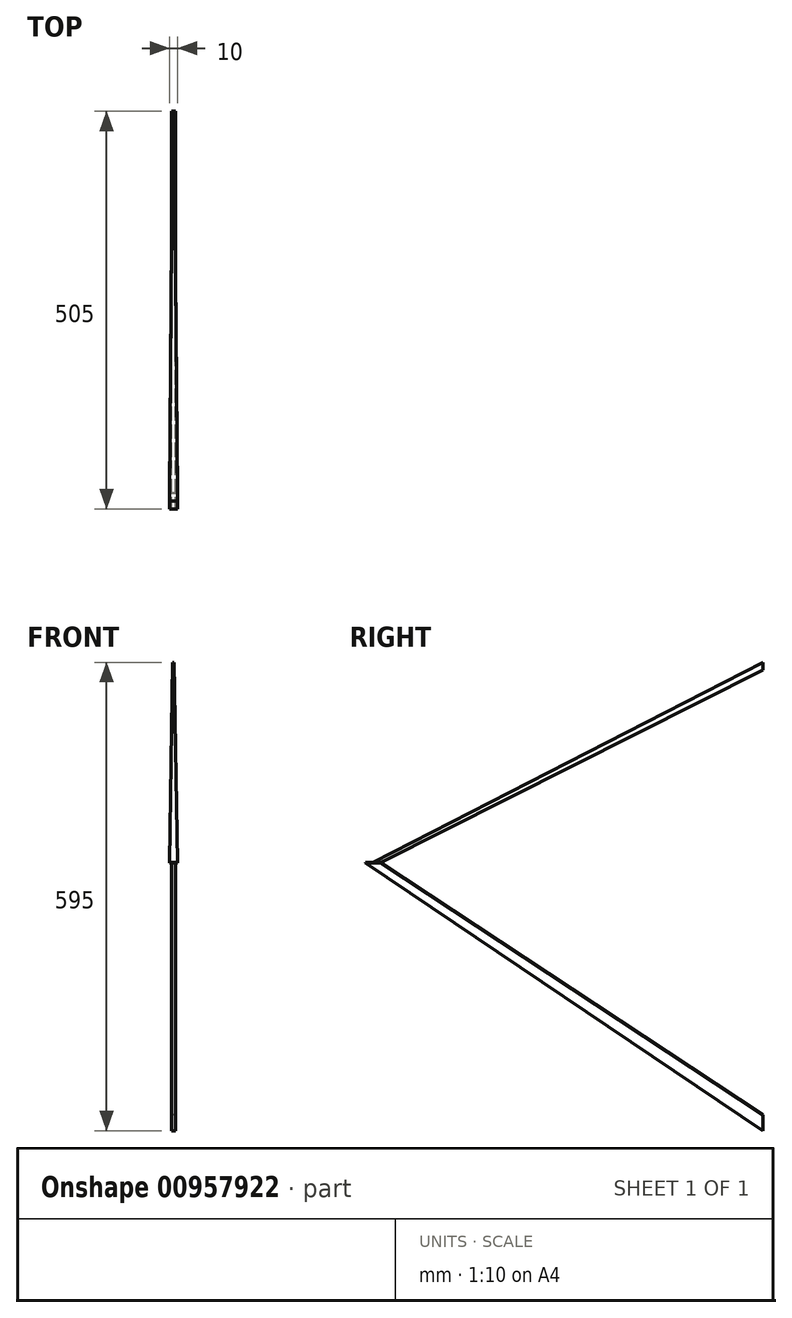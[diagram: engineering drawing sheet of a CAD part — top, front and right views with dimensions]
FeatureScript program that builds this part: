
annotation { "Feature Type Name" : "Feature", "Feature Type Description" : "" }
export const myFeature = defineFeature(function(context is Context, id is Id, definition is map)
    precondition{}
    {
        {
            var Q0;
            Q0=qCreatedBy(makeId("Top.planeOp"),FACE);
            var sketch = newSketch(context, id + "F0", { "sketchPlane" : qUnion([Q0])});
            skLineSegment(sketch, "E0.bottom", {"start": v(-49.59, 0) * mm, "end": v(-39.59, 0) * mm});
            skLineSegment(sketch, "E0.top", {"start": v(-49.59, -505) * mm, "end": v(-39.59, -505) * mm});
            skLineSegment(sketch, "E0.left", {"start": v(-49.59, 0) * mm, "end": v(-49.59, -505) * mm});
            skLineSegment(sketch, "E0.right", {"start": v(-39.59, 0) * mm, "end": v(-39.59, -505) * mm});
            skSolve(sketch);
        }
        {
            var Q0;
            Q0 = qSketchRegion(id + "F0", true);
            extrude(context, id + "F1", {"entities" : qUnion([Q0]), "depth" : 1 * mm, "offsetDistance" : 25 * mm});
        }
        {
            var Q0;
            Q0=makeQuery(id+"F1.opExtrude","CAP_FACE",FACE,{"disambiguationData":[OSD([sQuery(id+"F0.wireOp",EDGE,"E0.bottom"),sQuery(id+"F0.wireOp",EDGE,"E0.top"),sQuery(id+"F0.wireOp",EDGE,"E0.left"),sQuery(id+"F0.wireOp",EDGE,"E0.right")])],"isStart":false});
            var sketch = newSketch(context, id + "F2", { "sketchPlane" : qUnion([Q0])});
            skLineSegment(sketch, "E1.bottom", {"start": v(-49.59, -505) * mm, "end": v(-39.59, -505) * mm});
            skLineSegment(sketch, "E1.top", {"start": v(-49.59, -495) * mm, "end": v(-39.59, -495) * mm});
            skLineSegment(sketch, "E1.left", {"start": v(-49.59, -505) * mm, "end": v(-49.59, -495) * mm});
            skLineSegment(sketch, "E1.right", {"start": v(-39.59, -505) * mm, "end": v(-39.59, -495) * mm});
            skSolve(sketch);
        }
        {
            var Q0;
            Q0=makeQuery(id+"F1.opExtrude","CAP_FACE",FACE,{"disambiguationData":[OSD([sQuery(id+"F0.wireOp",EDGE,"E0.bottom"),sQuery(id+"F0.wireOp",EDGE,"E0.top"),sQuery(id+"F0.wireOp",EDGE,"E0.left"),sQuery(id+"F0.wireOp",EDGE,"E0.right")])],"isStart":true});
            var sketch = newSketch(context, id + "F3", { "sketchPlane" : qUnion([Q0])});
            skLineSegment(sketch, "E2.bottom", {"start": v(-41.87, 505) * mm, "end": v(-47.3, 505) * mm});
            skLineSegment(sketch, "E2.top", {"start": v(-41.87, 485) * mm, "end": v(-47.3, 485) * mm});
            skLineSegment(sketch, "E2.left", {"start": v(-41.87, 505) * mm, "end": v(-41.87, 485) * mm});
            skLineSegment(sketch, "E2.right", {"start": v(-47.3, 505) * mm, "end": v(-47.3, 485) * mm});
            skSolve(sketch);
        }
        {
            var Q0;
            Q0=qCreatedBy(makeId("Front.planeOp"),FACE);
            var sketch = newSketch(context, id + "F4", { "sketchPlane" : qUnion([Q0])});
            skPoint(sketch, "E3", {"position": v(-44.59, 0) * mm});
            skLineSegment(sketch, "E4", {"start": v(-44.59, 0) * mm, "end": v(-44.59, -330) * mm});
            skLineSegment(sketch, "E5.bottom", {"start": v(-42.09, -320) * mm, "end": v(-47.09, -320) * mm});
            skLineSegment(sketch, "E5.top", {"start": v(-42.09, -340) * mm, "end": v(-47.09, -340) * mm});
            skLineSegment(sketch, "E5.left", {"start": v(-42.09, -320) * mm, "end": v(-42.09, -340) * mm});
            skLineSegment(sketch, "E5.right", {"start": v(-47.09, -320) * mm, "end": v(-47.09, -340) * mm});
            skPoint(sketch, "E5.middle", {"position": v(-44.59, -330) * mm});
            skLineSegment(sketch, "E6", {"start": v(-44.59, 0) * mm, "end": v(-44.59, 250) * mm});
            skSolve(sketch);
        }
        {
            var Q1;
            Q1 = qSketchRegion(id + "F3", true);
            var Q2;
            Q2 = qSketchRegion(id + "F4", true);
            loft(context, id + "F5", {"operationType" : NewBodyOperationType.ADD, "sheetProfilesArray" : [{ "sheetProfileEntities" : qUnion([Q1]) }, { "sheetProfileEntities" : qUnion([Q2]) }]});
        }
        {
            var Q0;
            Q0=qCreatedBy(makeId("Front.planeOp"),FACE);
            var sketch = newSketch(context, id + "F6", { "sketchPlane" : qUnion([Q0])});
            skLineSegment(sketch, "E7.bottom", {"start": v(-45.59, 255) * mm, "end": v(-43.59, 255) * mm});
            skLineSegment(sketch, "E7.top", {"start": v(-45.59, 245) * mm, "end": v(-43.59, 245) * mm});
            skLineSegment(sketch, "E7.left", {"start": v(-45.59, 255) * mm, "end": v(-45.59, 245) * mm});
            skLineSegment(sketch, "E7.right", {"start": v(-43.59, 255) * mm, "end": v(-43.59, 245) * mm});
            skPoint(sketch, "E7.middle", {"position": v(-44.59, 250) * mm});
            skSolve(sketch);
        }
        {
            var Q0;
            {var subQ0=sQuery(id+"F2.wireOp",EDGE,"E1.top");Q0=makeQuery(id+"F2.imprint","IMPRINT",FACE,{"disambiguationData":[TD([[makeQuery(id+"F2.imprint","IMPRINT",EDGE,{"derivedFrom":subQ0}),1.0]])]});}
            var sketch = newSketch(context, id + "F7", { "sketchPlane" : qUnion([Q0])});
            skLineSegment(sketch, "E8.bottom", {"start": v(-49.59, -494.97) * mm, "end": v(-39.59, -494.97) * mm});
            skLineSegment(sketch, "E8.top", {"start": v(-49.59, -484.97) * mm, "end": v(-39.59, -484.97) * mm});
            skLineSegment(sketch, "E8.left", {"start": v(-49.59, -494.97) * mm, "end": v(-49.59, -484.97) * mm});
            skLineSegment(sketch, "E8.right", {"start": v(-39.59, -494.97) * mm, "end": v(-39.59, -484.97) * mm});
            skSolve(sketch);
        }
        {
            var Q1;
            Q1 = qSketchRegion(id + "F7", true);
            var Q2;
            Q2 = qSketchRegion(id + "F6", true);
            loft(context, id + "F8", {"operationType" : NewBodyOperationType.ADD, "sheetProfilesArray" : [{ "sheetProfileEntities" : qUnion([Q1]) }, { "sheetProfileEntities" : qUnion([Q2]) }]});
        }
        {
            var Q0;
            Q0=makeQuery(id+"F1.opExtrude","SWEPT_FACE",FACE,{"disambiguationData":[OSD([sQuery(id+"F0.wireOp",EDGE,"E0.right")])]});
            var sketch = newSketch(context, id + "F9", { "sketchPlane" : qUnion([Q0])});
            skLineSegment(sketch, "E9.bottom", {"start": v(-484.97, 1) * mm, "end": v(0, 1) * mm});
            skLineSegment(sketch, "E9.top", {"start": v(-484.97, 0) * mm, "end": v(0, 0) * mm});
            skLineSegment(sketch, "E9.left", {"start": v(-484.97, 1) * mm, "end": v(-484.97, 0) * mm});
            skLineSegment(sketch, "E9.right", {"start": v(0, 1) * mm, "end": v(0, 0) * mm});
            skLineSegment(sketch, "E10.bottom", {"start": v(0, 0) * mm, "end": v(0, 0) * mm});
            skLineSegment(sketch, "E10.top", {"start": v(0, 0) * mm, "end": v(0, 0) * mm});
            skLineSegment(sketch, "E10.left", {"start": v(0, 0) * mm, "end": v(0, 0) * mm});
            skLineSegment(sketch, "E10.right", {"start": v(0, 0) * mm, "end": v(0, 0) * mm});
            skSolve(sketch);
        }
        {
            var Q0;
            Q0 = qSketchRegion(id + "F9", true);
            extrude(context, id + "F10", {"entities" : qUnion([Q0]), "operationType" : NewBodyOperationType.REMOVE, "endBound" : BoundingType.THROUGH_ALL, "oppositeDirection" : true, "depth" : 25 * mm, "offsetDistance" : 25 * mm});
        }
    });
